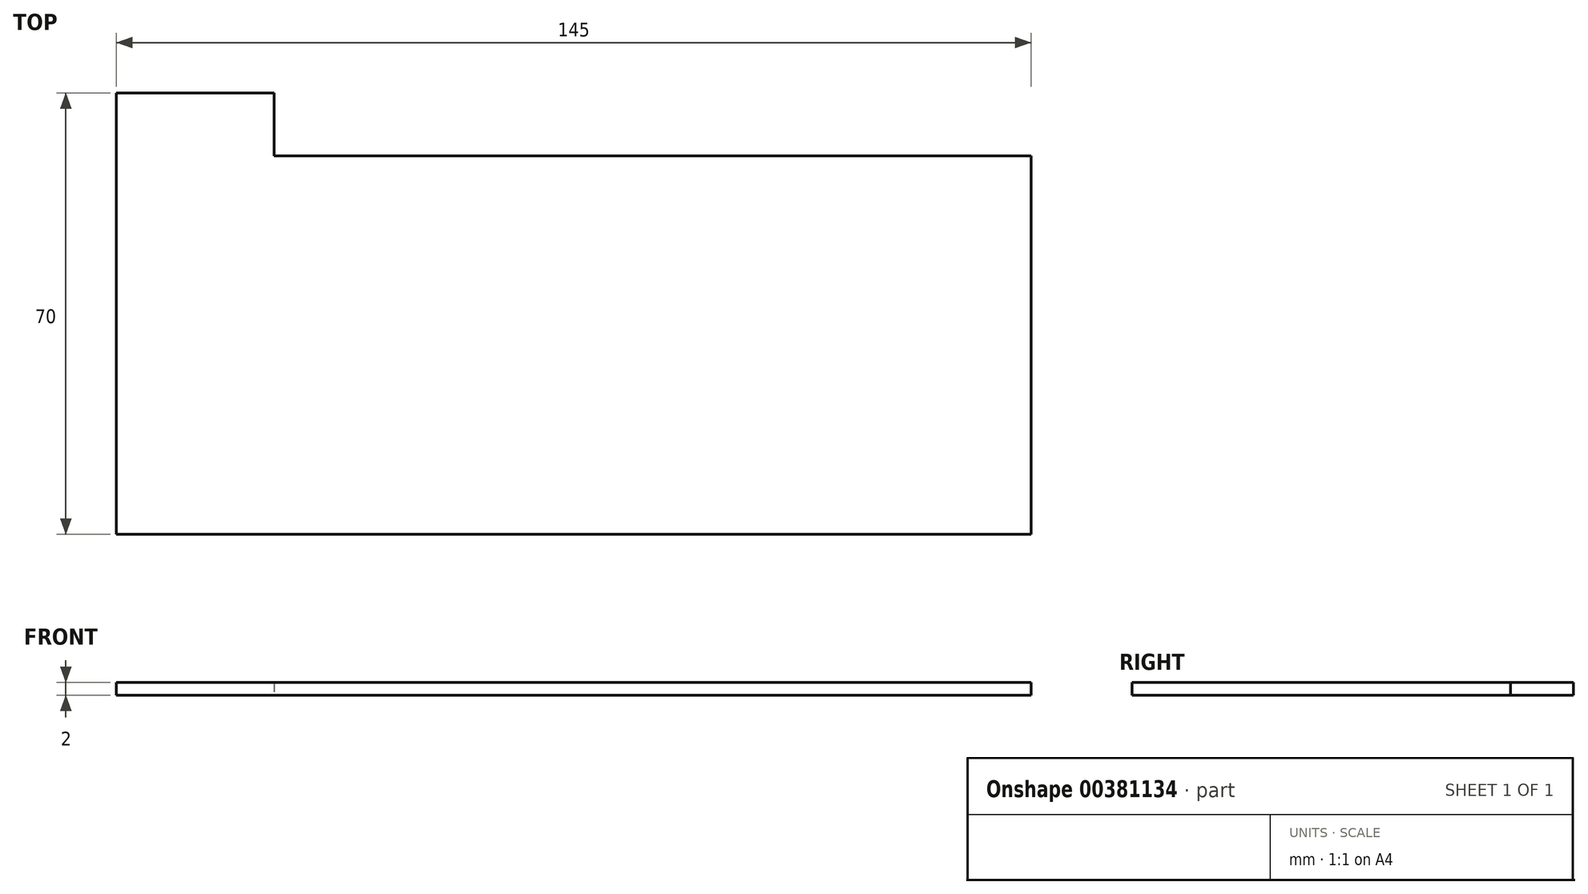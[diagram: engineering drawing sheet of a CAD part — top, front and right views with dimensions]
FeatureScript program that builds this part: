
annotation { "Feature Type Name" : "Feature", "Feature Type Description" : "" }
export const myFeature = defineFeature(function(context is Context, id is Id, definition is map)
    precondition{}
    {
        {
            var Q0;
            Q0=qCreatedBy(makeId("Top.planeOp"),FACE);
            var sketch = newSketch(context, id + "F0", { "sketchPlane" : qUnion([Q0])});
            skLineSegment(sketch, "E0.bottom", {"start": v(72.5, -30) * mm, "end": v(-72.5, -30) * mm});
            skLineSegment(sketch, "E0.top", {"start": v(72.5, 30) * mm, "end": v(-47.5, 30) * mm});
            skLineSegment(sketch, "E0.left", {"start": v(72.5, -30) * mm, "end": v(72.5, 30) * mm});
            skLineSegment(sketch, "E0.right", {"start": v(-72.5, -30) * mm, "end": v(-72.5, 30) * mm});
            skPoint(sketch, "E0.middle", {"position": v(0, 0) * mm});
            skLineSegment(sketch, "E1", {"start": v(-72.5, 30) * mm, "end": v(-72.5, 40) * mm});
            skLineSegment(sketch, "E2", {"start": v(-72.5, 40) * mm, "end": v(-47.5, 40) * mm});
            skLineSegment(sketch, "E3", {"start": v(-47.5, 40) * mm, "end": v(-47.5, 30) * mm});
            skSolve(sketch);
        }
        {
            var Q0;
            Q0 = qSketchRegion(id + "F0", true);
            extrude(context, id + "F1", {"entities" : qUnion([Q0]), "depth" : 2 * mm});
        }
    });
